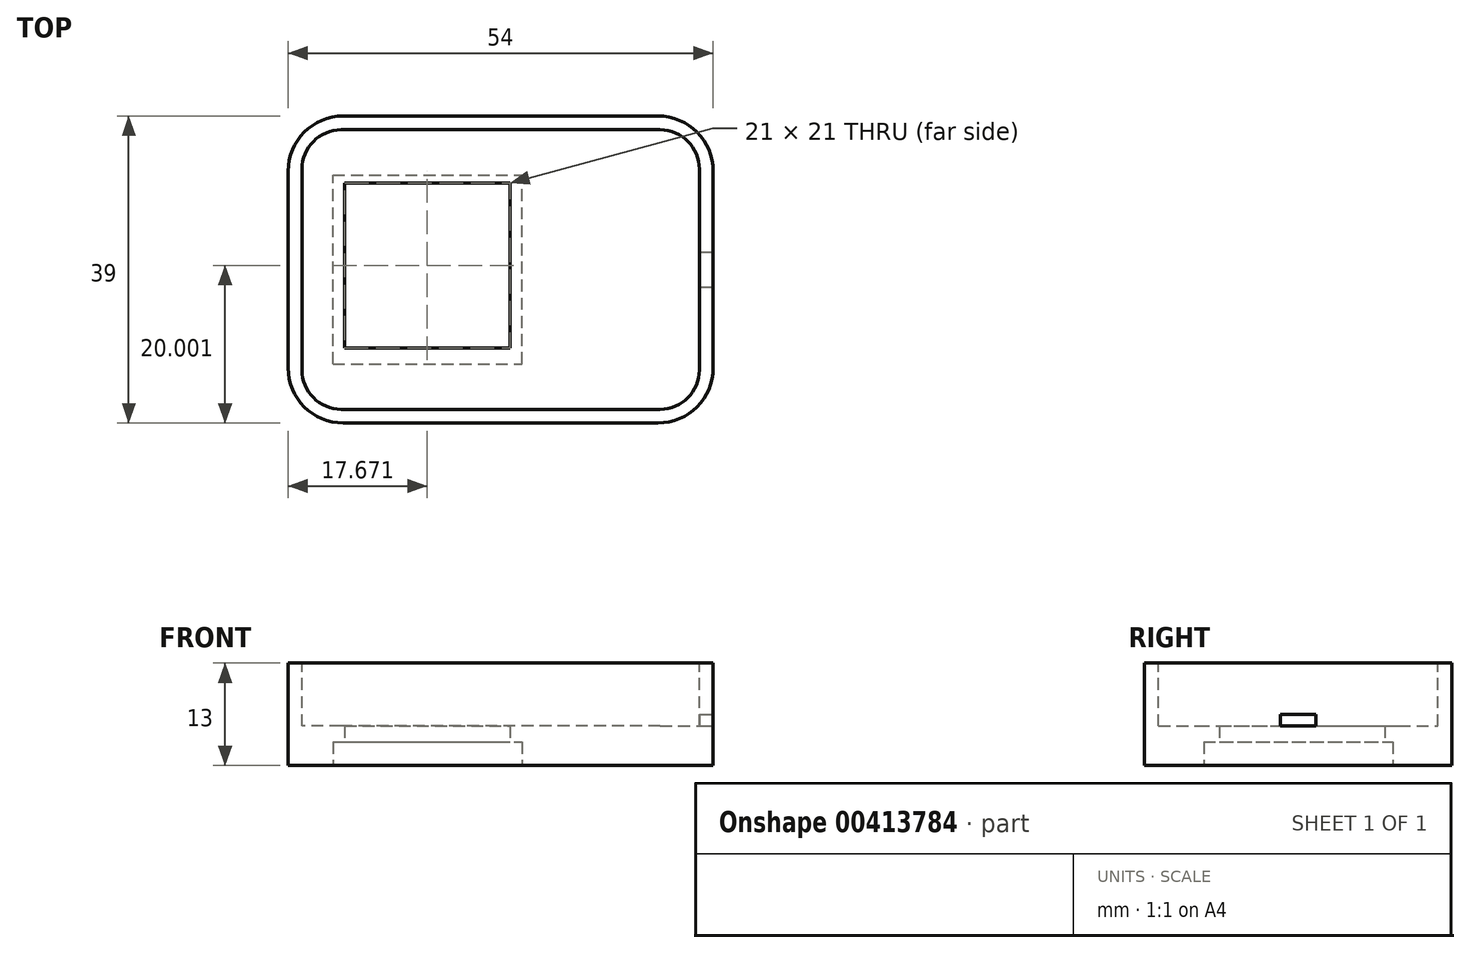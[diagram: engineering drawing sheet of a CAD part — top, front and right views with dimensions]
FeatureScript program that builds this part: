
annotation { "Feature Type Name" : "Feature", "Feature Type Description" : "" }
export const myFeature = defineFeature(function(context is Context, id is Id, definition is map)
    precondition{}
    {
        {
            var Q0;
            Q0=qCreatedBy(makeId("Top.planeOp"),FACE);
            var sketch = newSketch(context, id + "F0", { "sketchPlane" : qUnion([Q0])});
            skLineSegment(sketch, "E0.bottom", {"start": v(27, -19.5) * mm, "end": v(-27, -19.5) * mm});
            skLineSegment(sketch, "E0.top", {"start": v(27, 19.5) * mm, "end": v(-27, 19.5) * mm});
            skLineSegment(sketch, "E0.left", {"start": v(27, -19.5) * mm, "end": v(27, 19.5) * mm});
            skLineSegment(sketch, "E0.right", {"start": v(-27, -19.5) * mm, "end": v(-27, 19.5) * mm});
            skPoint(sketch, "E0.middle", {"position": v(0, 0) * mm});
            skSolve(sketch);
        }
        {
            var Q0;
            Q0=makeQuery(id+"F0.imprint","IMPRINT",FACE,{"disambiguationData":[TD([[makeQuery(id+"F0.imprint","IMPRINT",EDGE,{"derivedFrom":sQuery(id+"F0.wireOp",EDGE,"E0.bottom")}),-1.0]])]});
            extrude(context, id + "F1", {"entities" : qUnion([Q0]), "depth" : 13 * mm});
        }
        {
            var Q0;
            Q0=makeQuery(id+"F1.opExtrude","CAP_FACE",FACE,{"disambiguationData":[OSD([sQuery(id+"F0.wireOp",EDGE,"E0.bottom"),sQuery(id+"F0.wireOp",EDGE,"E0.top"),sQuery(id+"F0.wireOp",EDGE,"E0.left"),sQuery(id+"F0.wireOp",EDGE,"E0.right")])],"isStart":false});
            var sketch = newSketch(context, id + "F2", { "sketchPlane" : qUnion([Q0])});
            skLineSegment(sketch, "E1.bottom", {"start": v(25.25, -17.75) * mm, "end": v(-25.25, -17.75) * mm});
            skLineSegment(sketch, "E1.top", {"start": v(25.25, 17.75) * mm, "end": v(-25.25, 17.75) * mm});
            skLineSegment(sketch, "E1.left", {"start": v(25.25, -17.75) * mm, "end": v(25.25, 17.75) * mm});
            skLineSegment(sketch, "E1.right", {"start": v(-25.25, -17.75) * mm, "end": v(-25.25, 17.75) * mm});
            skPoint(sketch, "E1.middle", {"position": v(0, 0) * mm});
            skSolve(sketch);
        }
        {
            var Q0;
            Q0=makeQuery(id+"F2.imprint","IMPRINT",FACE,{"disambiguationData":[TD([[makeQuery(id+"F2.imprint","IMPRINT",EDGE,{"derivedFrom":sQuery(id+"F2.wireOp",EDGE,"E1.bottom")}),-1.0]])]});
            extrude(context, id + "F3", {"entities" : qUnion([Q0]), "operationType" : NewBodyOperationType.REMOVE, "oppositeDirection" : true, "depth" : 8 * mm});
        }
        {
            var Q0;
            Q0=makeQuery(id+"F1.opExtrude","CAP_FACE",FACE,{"disambiguationData":[OSD([sQuery(id+"F0.wireOp",EDGE,"E0.bottom"),sQuery(id+"F0.wireOp",EDGE,"E0.top"),sQuery(id+"F0.wireOp",EDGE,"E0.left"),sQuery(id+"F0.wireOp",EDGE,"E0.right")])],"isStart":true});
            var sketch = newSketch(context, id + "F4", { "sketchPlane" : qUnion([Q0])});
            skLineSegment(sketch, "E2.bottom", {"start": v(-21.3, 12) * mm, "end": v(2.7, 12) * mm});
            skLineSegment(sketch, "E2.top", {"start": v(-21.3, -12) * mm, "end": v(2.7, -12) * mm});
            skLineSegment(sketch, "E2.left", {"start": v(-21.3, 12) * mm, "end": v(-21.3, -12) * mm});
            skLineSegment(sketch, "E2.right", {"start": v(2.7, 12) * mm, "end": v(2.7, -12) * mm});
            skSolve(sketch);
        }
        {
            var Q0;
            Q0=makeQuery(id+"F4.imprint","IMPRINT",FACE,{"disambiguationData":[TD([[makeQuery(id+"F4.imprint","IMPRINT",EDGE,{"derivedFrom":sQuery(id+"F4.wireOp",EDGE,"E2.bottom")}),-1.0]])]});
            extrude(context, id + "F5", {"entities" : qUnion([Q0]), "operationType" : NewBodyOperationType.REMOVE, "oppositeDirection" : true, "depth" : 3 * mm});
        }
        {
            var Q0;
            Q0=makeQuery(id+"F5.boolean.opBoolean","COPY",FACE,{"derivedFrom":makeQuery(id+"F5.opExtrude","CAP_FACE",FACE,{"disambiguationData":[OSD([sQuery(id+"F4.wireOp",EDGE,"E2.bottom"),sQuery(id+"F4.wireOp",EDGE,"E2.top"),sQuery(id+"F4.wireOp",EDGE,"E2.left"),sQuery(id+"F4.wireOp",EDGE,"E2.right")])],"isStart":false})});
            var sketch = newSketch(context, id + "F6", { "sketchPlane" : qUnion([Q0])});
            skLineSegment(sketch, "E3.bottom", {"start": v(-19.83, 10) * mm, "end": v(1.17, 10) * mm});
            skLineSegment(sketch, "E3.top", {"start": v(-19.83, -11) * mm, "end": v(1.17, -11) * mm});
            skLineSegment(sketch, "E3.left", {"start": v(-19.83, 10) * mm, "end": v(-19.83, -11) * mm});
            skLineSegment(sketch, "E3.right", {"start": v(1.17, 10) * mm, "end": v(1.17, -11) * mm});
            skSolve(sketch);
        }
        {
            var Q0;
            Q0=makeQuery(id+"F6.imprint","IMPRINT",FACE,{"disambiguationData":[TD([[makeQuery(id+"F6.imprint","IMPRINT",EDGE,{"derivedFrom":sQuery(id+"F6.wireOp",EDGE,"E3.bottom")}),-1.0]])]});
            extrude(context, id + "F7", {"entities" : qUnion([Q0]), "operationType" : NewBodyOperationType.REMOVE, "oppositeDirection" : true, "depth" : 2 * mm});
        }
        {
            var Q0;
            Q0=makeQuery(id+"F3.boolean.opBoolean","COPY",EDGE,{"derivedFrom":makeQuery(id+"F3.opExtrude","SWEPT_EDGE",EDGE,{"disambiguationData":[OSD([sQuery(id+"F2.wireOp",EDGE,"E1.top"),sQuery(id+"F2.wireOp",EDGE,"E1.right")])]})});
            var Q1;
            Q1=makeQuery(id+"F3.boolean.opBoolean","COPY",EDGE,{"derivedFrom":makeQuery(id+"F3.opExtrude","SWEPT_EDGE",EDGE,{"disambiguationData":[OSD([sQuery(id+"F2.wireOp",EDGE,"E1.top"),sQuery(id+"F2.wireOp",EDGE,"E1.left")])]})});
            var Q2;
            Q2=makeQuery(id+"F3.boolean.opBoolean","COPY",EDGE,{"derivedFrom":makeQuery(id+"F3.opExtrude","SWEPT_EDGE",EDGE,{"disambiguationData":[OSD([sQuery(id+"F2.wireOp",EDGE,"E1.bottom"),sQuery(id+"F2.wireOp",EDGE,"E1.right")])]})});
            var Q3;
            Q3=makeQuery(id+"F3.boolean.opBoolean","COPY",EDGE,{"derivedFrom":makeQuery(id+"F3.opExtrude","SWEPT_EDGE",EDGE,{"disambiguationData":[OSD([sQuery(id+"F2.wireOp",EDGE,"E1.bottom"),sQuery(id+"F2.wireOp",EDGE,"E1.left")])]})});
            fillet(context, id + "F8", {"entities" : qUnion([Q0, Q1, Q2, Q3]), "radius" : 5 * mm, "tangentPropagation" : true, "allowEdgeOverflow" : false});
        }
        {
            var Q0;
            Q0=makeQuery(id+"F1.opExtrude","SWEPT_EDGE",EDGE,{"disambiguationData":[OSD([sQuery(id+"F0.wireOp",EDGE,"E0.top"),sQuery(id+"F0.wireOp",EDGE,"E0.right")])]});
            var Q1;
            Q1=makeQuery(id+"F1.opExtrude","SWEPT_EDGE",EDGE,{"disambiguationData":[OSD([sQuery(id+"F0.wireOp",EDGE,"E0.bottom"),sQuery(id+"F0.wireOp",EDGE,"E0.right")])]});
            var Q2;
            Q2=makeQuery(id+"F1.opExtrude","SWEPT_EDGE",EDGE,{"disambiguationData":[OSD([sQuery(id+"F0.wireOp",EDGE,"E0.top"),sQuery(id+"F0.wireOp",EDGE,"E0.left")])]});
            var Q3;
            Q3=makeQuery(id+"F1.opExtrude","SWEPT_EDGE",EDGE,{"disambiguationData":[OSD([sQuery(id+"F0.wireOp",EDGE,"E0.bottom"),sQuery(id+"F0.wireOp",EDGE,"E0.left")])]});
            fillet(context, id + "F9", {"entities" : qUnion([Q0, Q1, Q2, Q3]), "radius" : 7 * mm, "tangentPropagation" : true, "allowEdgeOverflow" : false});
        }
        {
            var Q0;
            Q0=makeQuery(id+"F1.opExtrude","SWEPT_FACE",FACE,{"disambiguationData":[OSD([sQuery(id+"F0.wireOp",EDGE,"E0.left")])]});
            var sketch = newSketch(context, id + "F10", { "sketchPlane" : qUnion([Q0])});
            skLineSegment(sketch, "E4.bottom", {"start": v(-2.25, 6.5) * mm, "end": v(2.25, 6.5) * mm});
            skLineSegment(sketch, "E4.top", {"start": v(-2.25, 5) * mm, "end": v(2.25, 5) * mm});
            skLineSegment(sketch, "E4.left", {"start": v(-2.25, 6.5) * mm, "end": v(-2.25, 5) * mm});
            skLineSegment(sketch, "E4.right", {"start": v(2.25, 6.5) * mm, "end": v(2.25, 5) * mm});
            skSolve(sketch);
        }
        {
            var Q0;
            Q0=makeQuery(id+"F10.imprint","IMPRINT",FACE,{"disambiguationData":[TD([[makeQuery(id+"F10.imprint","IMPRINT",EDGE,{"derivedFrom":sQuery(id+"F10.wireOp",EDGE,"E4.bottom")}),-1.0]])]});
            extrude(context, id + "F11", {"entities" : qUnion([Q0]), "operationType" : NewBodyOperationType.REMOVE, "oppositeDirection" : true, "depth" : 1.75 * mm});
        }
    });
